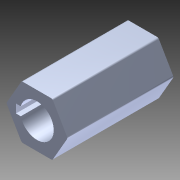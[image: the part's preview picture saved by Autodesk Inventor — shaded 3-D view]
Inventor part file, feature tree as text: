
AUTODESK INVENTOR PART (.ipt)
format: ipt  version: 2014 SP1 (Build 180222100, 222)  size: 112,128 bytes
history: native  units: in
note: dims shown in document units (in); Inventor stores cm internally (conversion verified against a paired STEP export)
features: fillet x1, other x1, imported_body x1
ambient origin geometry x8: Origin, YZ Plane, XZ Plane, XY Plane, X Axis, Y Axis, Z Axis, Center Point
bodies: Body1 (feature_tree)
feature tree (3):
  fillet  "Fillet1"  [1 undecoded]
  other  "8mm to .5 hex1"
  imported_body  "Base1"
note: 1 required parameter value undecoded (feature->parameter linkage not recoverable at this tier; creation-order binding heuristic only, values carry confidence <= 0.55)
